# Revit family: Tub_Spout-American_Standard-Serin-8888087.002
name_source: partatom
category: Plumbing Fixtures
revit_build: Autodesk Revit 2018 (Build: 20170223_1515(x64)
units: mm (PartAtom-declared; Revit-internal decimal feet)

## family parameters
Cut with Voids When Loaded = No
Host = Face
OmniClass Number = 23.45.05.14.21
OmniClass Title = Bathtubs
Part Type = Normal
Room Calculation Point = No
Round Connector Dimension = Use Diameter
Shared = Yes

## types (1)
- 8888087.002
    Assembly Code = D2020300
    CW Connection = No
    CWFU = 3
    Connection Size = 1/2"
    Default Elevation = 25"
    Description = Serin® 4-7/8-Inch Slip-On Diverter Tub Spout
    Finish = Brass-American Standard-002-Polished Chrome
    HW Connection = No
    HWFU = 3
    Installation Type = Wall Mounted
    Length = 4 7/8"
    Manufacturer = American Standard
    Material = Brass-American Standard-002-Polished Chrome
    Model = 8888087.002
    Price = Prices may vary. Please consult Manufacturer Representative for most up-to-date price list.
    Product Documentation Link = https://americanstandard.box.com
    Product Page URL = https://www.americanstandard-us.com
    Revised Date = 07/05/2022
    Tempered Water Connection = Yes
    URL = http://www.americanstandard-us.com
    Vent Connection = No
    WFU = 4
    Waste Connection = No

## geometry (parser evidence)
native form markers: Sweep x3
no freeform markers — native parametric forms only
